# Revit family: 3L-R-D
name_source: partatom
category: Lighting Fixtures
revit_build: Autodesk Revit 2013 (Build: 20130531_2115(x64)
units: mm (PartAtom-declared; Revit-internal decimal feet)

## types (1)
- 3L-R-D-4-SOF-X-CX-35K-D100
    Apparent Load = 10 VA
    Color Filter = 16777215
    Default Elevation = 4' - 0"
    Description = Mod™ 3 LED Recessed Slot
    Dimming Lamp Color Temperature Shift = <None>
    Downlight diffuse = Soft Diffuse Lens
    Emit Shape Visible in Rendering = No
    Emit from Rectangle Length = 3' - 11"
    Emit from Rectangle Width = 0' - 2 3/4"
    Fixture Option = 3L-R : Carbon Black
    Lamp = LED Lamp
    Length = 4' - 0"
    Load Classification = Lighting
    Manufacturer = Litecontrol Lighting
    Manufacturer Fax = 781-293-2849
    Model = 3L-R-D
    Photometric Web File = 3L-R-D-4-SOF-X-CX-35K-D100.IES
    Power Factor = 1
    Product Documentation Link = http://www.litecontrol.com
    Product Page URL = http://www.litecontrol.com
    Tilt Angle = -90.00°
    URL = http://www.litecontrol.com
    Voltage = 277 V
    Wattage Comments = Variable Intensity technology provides specifiable lumen output/wattage
    Watts = 10 W
    zzLength1 = 0' - 5 5/8"

## geometry (parser evidence)
native form markers: Blend x6, Sweep x4
no freeform markers — native parametric forms only
